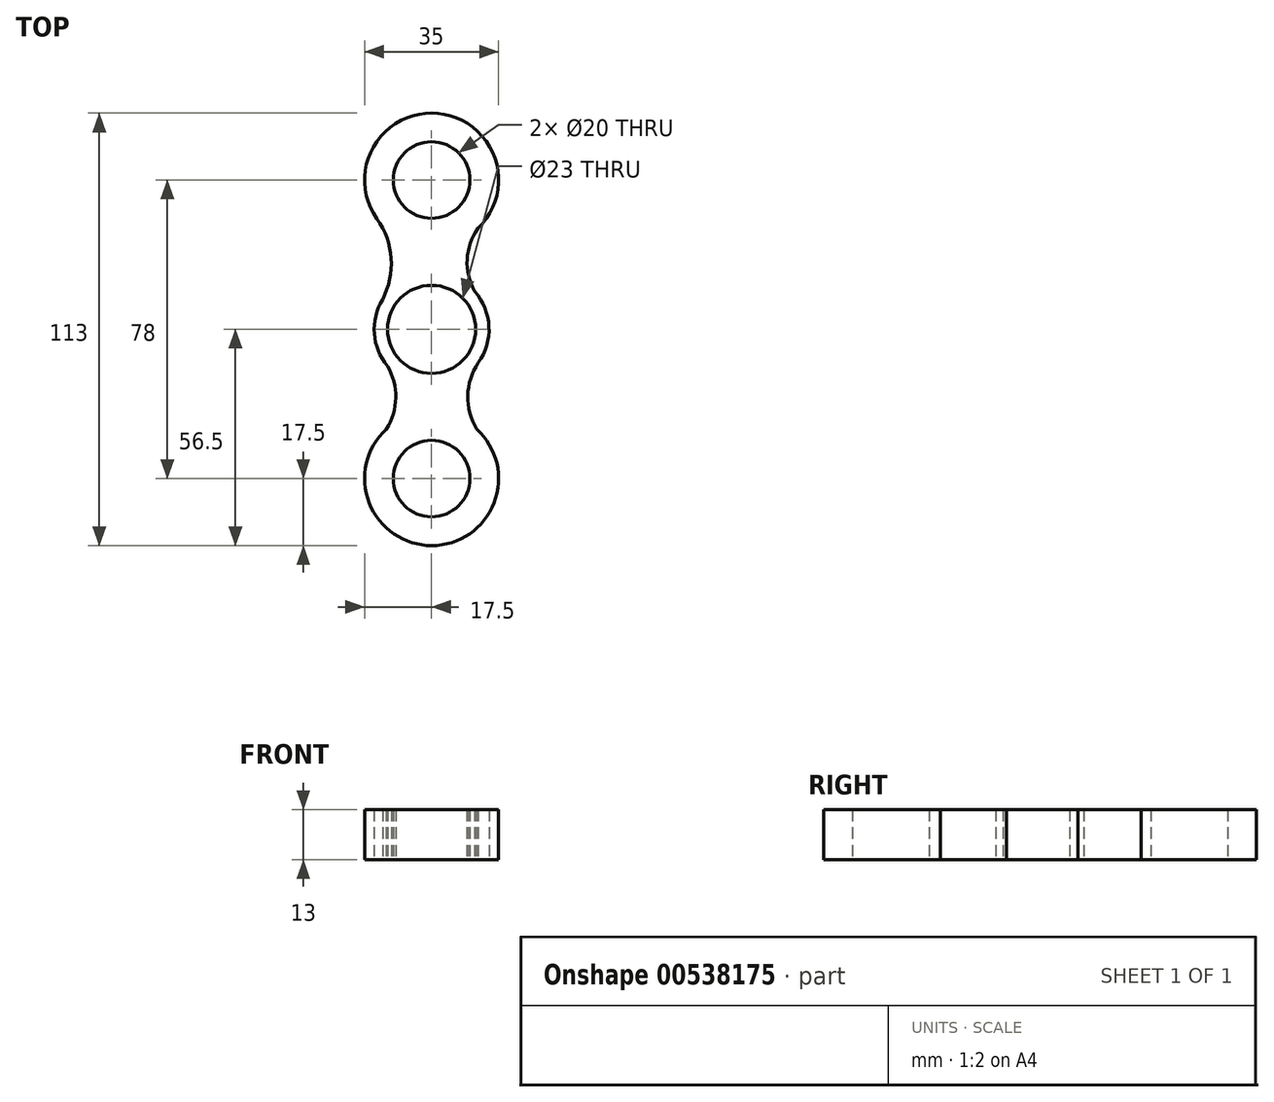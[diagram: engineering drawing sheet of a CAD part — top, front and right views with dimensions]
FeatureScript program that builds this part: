
annotation { "Feature Type Name" : "Feature", "Feature Type Description" : "" }
export const myFeature = defineFeature(function(context is Context, id is Id, definition is map)
    precondition{}
    {
        {
            var Q0;
            Q0=qCreatedBy(makeId("Top.planeOp"),FACE);
            var sketch = newSketch(context, id + "F0", { "sketchPlane" : qUnion([Q0])});
            skCircle(sketch, "E0", {"center": v(0, 0) * mm, "radius": 11.5 * mm});
            skCircle(sketch, "E1", {"center": v(0, 39) * mm, "radius": 10 * mm});
            skCircle(sketch, "E2", {"center": v(0, -39) * mm, "radius": 10 * mm});
            skCircle(sketch, "E3", {"center": v(0, 39) * mm, "radius": 17.5 * mm});
            skCircle(sketch, "E4", {"center": v(0, -39) * mm, "radius": 17.5 * mm});
            skCircle(sketch, "E5", {"center": v(0, 0) * mm, "radius": 15 * mm});
            skArc(sketch, "E6", {"start": v(-12.82, 7.8) * mm, "mid": v(-10.55, 18.52) * mm, "end": v(-14.25, 28.84) * mm});
            skArc(sketch, "E7", {"start": v(12.11, 26.37) * mm, "mid": v(9.28, 18.25) * mm, "end": v(11.28, 9.88) * mm});
            skArc(sketch, "E8", {"start": v(-11.84, -26.1) * mm, "mid": v(-9.37, -17.89) * mm, "end": v(-11.54, -9.58) * mm});
            skArc(sketch, "E9", {"start": v(12.18, -8.75) * mm, "mid": v(9.45, -17.35) * mm, "end": v(11.78, -26.06) * mm});
            skSolve(sketch);
        }
        {
            var Q0;
            Q0=makeQuery(id+"F0.imprint","IMPRINT",FACE,{"disambiguationData":[TD([[makeQuery(id+"F0.imprint","IMPRINT",EDGE,{"derivedFrom":sQuery(id+"F0.wireOp",EDGE,"E1")}),-1.0]])]});
            var Q1;
            Q1=makeQuery(id+"F0.imprint","IMPRINT",FACE,{"disambiguationData":[TD([[makeQuery(id+"F0.imprint","IMPRINT",EDGE,{"derivedFrom":sQuery(id+"F0.wireOp",EDGE,"E0")}),-1.0]])]});
            var Q2;
            Q2 = qSketchRegion(id + "F0", true);
            var Q3;
            {var subQ0=sQuery(id+"F0.wireOp",EDGE,"E8");Q3=makeQuery(id+"F0.imprint","IMPRINT",FACE,{"disambiguationData":[TD([[makeQuery(id+"F0.imprint","IMPRINT",EDGE,{"derivedFrom":subQ0}),-1.0]])]});}
            var Q4;
            {var subQ0=sQuery(id+"F0.wireOp",EDGE,"E6");Q4=makeQuery(id+"F0.imprint","IMPRINT",FACE,{"disambiguationData":[TD([[makeQuery(id+"F0.imprint","IMPRINT",EDGE,{"derivedFrom":subQ0}),-1.0]])]});}
            extrude(context, id + "F1", {"entities" : qUnion([Q0, Q1, Q2, Q3, Q4]), "depth" : 13 * mm, "offsetDistance" : 25 * mm});
        }
    });
